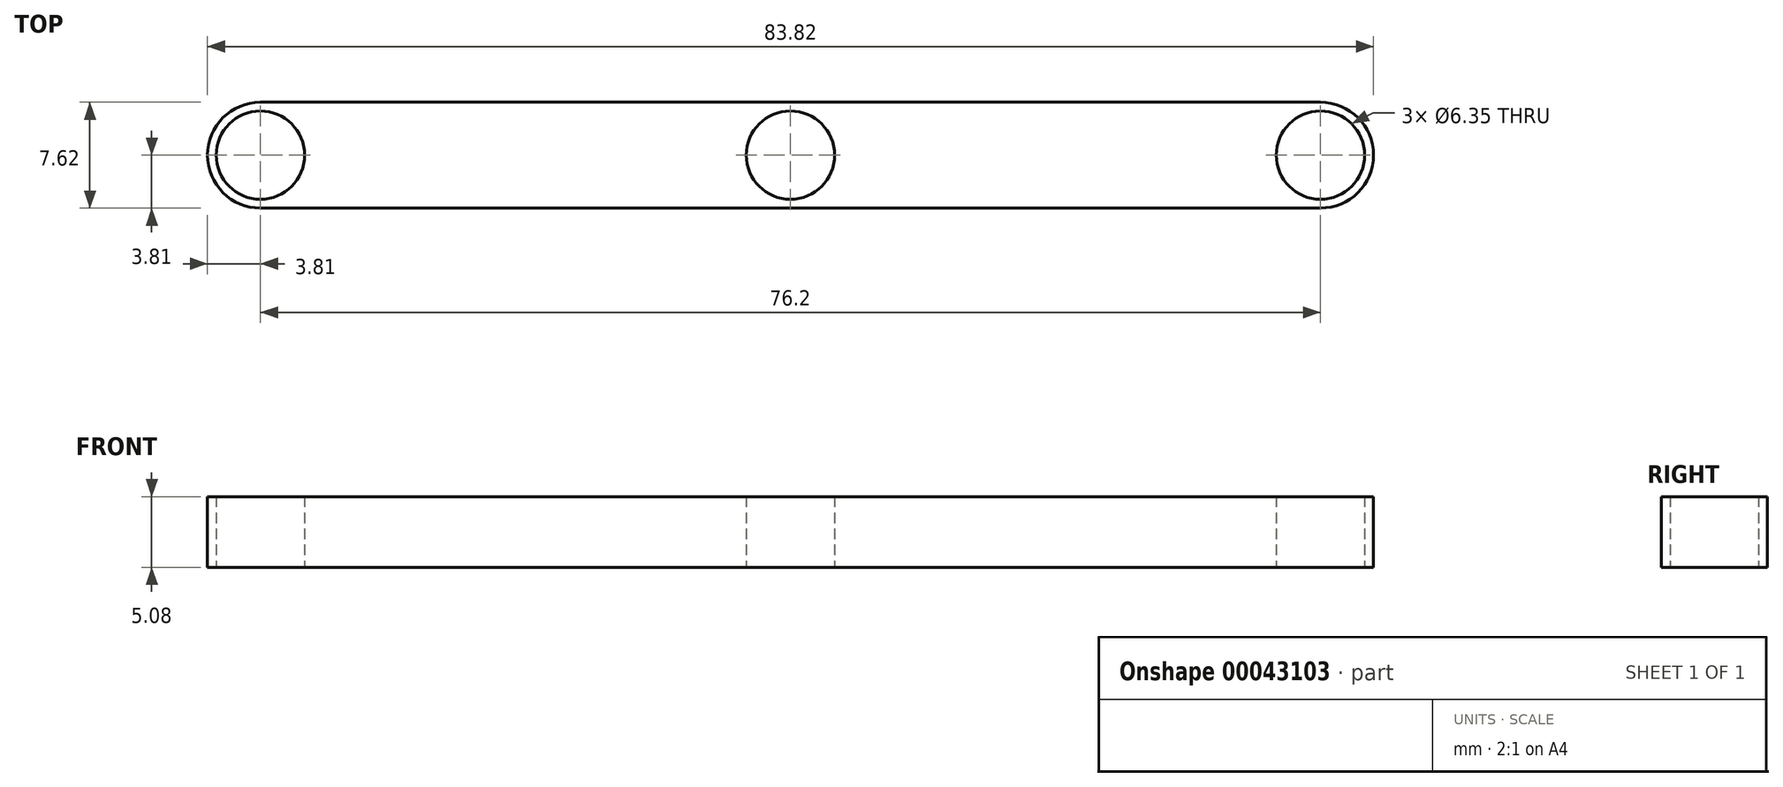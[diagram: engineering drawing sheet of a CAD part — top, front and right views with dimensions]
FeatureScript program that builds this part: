
annotation { "Feature Type Name" : "Feature", "Feature Type Description" : "" }
export const myFeature = defineFeature(function(context is Context, id is Id, definition is map)
    precondition{}
    {
        {
            var Q0;
            Q0=qCreatedBy(makeId("Top.planeOp"),FACE);
            var sketch = newSketch(context, id + "F0", { "sketchPlane" : qUnion([Q0])});
            skLineSegment(sketch, "E0.rect.bottom", {"start": v(38.1, -3.8) * mm, "end": v(-38.1, -3.81) * mm});
            skLineSegment(sketch, "E0.rect.top", {"start": v(38.1, 3.81) * mm, "end": v(-38.1, 3.8) * mm});
            skLineSegment(sketch, "E0.rect.left", {"start": v(38.1, -3.8) * mm, "end": v(38.1, 3.81) * mm});
            skLineSegment(sketch, "E0.rect.right", {"start": v(-38.1, -3.81) * mm, "end": v(-38.1, 3.8) * mm});
            skPoint(sketch, "E0.rect.middle", {"position": v(0, 0) * mm});
            skArc(sketch, "E1", {"start": v(38.1, -3.8) * mm, "mid": v(41.91, 0) * mm, "end": v(38.1, 3.81) * mm});
            skArc(sketch, "E2", {"start": v(-38.1, 3.8) * mm, "mid": v(-41.91, 0) * mm, "end": v(-38.1, -3.81) * mm});
            skCircle(sketch, "E3", {"center": v(38.1, 0) * mm, "radius": 3.18 * mm});
            skCircle(sketch, "E4", {"center": v(-38.1, 0) * mm, "radius": 3.18 * mm});
            skCircle(sketch, "E5", {"center": v(0, 0) * mm, "radius": 3.18 * mm});
            skSolve(sketch);
        }
        {
            var Q0;
            Q0 = qSketchRegion(id + "F0", true);
            extrude(context, id + "F1", {"entities" : qUnion([Q0]), "depth" : 5.08 * mm});
        }
    });
